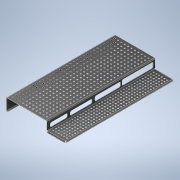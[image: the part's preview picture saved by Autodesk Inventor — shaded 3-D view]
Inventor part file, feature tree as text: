
AUTODESK INVENTOR PART (.ipt)
format: ipt  version: 2022 (Build 260153000, 153)  size: 1,057,280 bytes
history: native  units: in
note: dims shown in document units (in); Inventor stores cm internally (conversion verified against a paired STEP export)
features: sheet_metal_op x16, sketch x9, other x9
ambient origin geometry x8: Origin, YZ Plane, XZ Plane, XY Plane, X Axis, Y Axis, Z Axis, Center Point
bodies: Body1 (feature_tree)
feature tree (34):
  sheet_metal_op  "Face2"
  sheet_metal_op  "Flange1"
  sheet_metal_op  "Flange2"
  sheet_metal_op  "Flange3"
  sheet_metal_op  "Flange4"
  sheet_metal_op  "Flange9"
  sketch  "Sketch1"  dims[d2=5.5118in]
  other  "Plate2"
  sketch  "Sketch2"  dims[d3=2.7559in]
  other  "Plate3"
  sheet_metal_op  "Bend1"
  sheet_metal_op  "Corner1"
  sketch  "Sketch3"  dims[d8=0.1181in]
  other  "Plate4"
  sheet_metal_op  "Bend2"
  sheet_metal_op  "Corner2"
  sketch  "Sketch4"  dims[d9=0.1181in]
  other  "Plate5"
  sheet_metal_op  "Bend3"
  sheet_metal_op  "Corner3"
  sketch  "Sketch5"  dims[d10=0.0591in]
  other  "Plate6"
  sheet_metal_op  "Bend4"
  sheet_metal_op  "Corner4"
  sketch  "Sketch11"  dims[d11=0.2362in]
  sketch  "Sketch12"  dims[d12=0.1181in]
  sketch  "Sketch13"  dims[d13=2.7559in d14=90.0deg d15=0.1181in]
  sketch  "Sketch16"  dims[d16=0.4724in d17=0.1181in d18=0.1181in d19=0.1181in d20=0.0591in d21=0.2362in d22=0.1181in d23=11.811in d24=90.0deg d25=0.1181in d26=0.4724in d27=0.1181in d28=0.1181in d29=0.1181in d30=0.0591in d31=0.2362in d32=0.1181in d33=3.5433in d34=90.0deg d35=0.1181in d36=0.4724in d37=0.1181in d38=0.1181in d39=0.1181in d40=0.0591in d41=0.2362in d42=0.1181in d43=0.3937in d44=90.0deg d45=0.1181in d46=0.4724in d47=0.1181in d48=0.1181in d91=31.4961in d92=15.748in d93=1.5748in d94=0.3937in d95=0.5906in d97=0.3937in d98=7.4803in d100=9.0551in d101=0.7874in d102=0.7874in d103=0.9843in d104=0.3937in d105=1.1811in d106=6.399in d107=0.3937in d108=0.1181in d109=0.0in d110=1.378in d111=0.3937in d112=0.9843in d113=0.748in d114=12.2047in d116=0.9843in d117=4.3307in d119=0.9843in d122=0.9843in d123=0.748in d124=0.1181in d125=0.0in d126=0.3937in d128=0.9843in d130=0.5906in d131=14.9606in d133=0.7874in d134=2.3622in d136=0.7874in d141=0.1181in d142=0.0in d147=1.1811in d148=1.1811in d149=0.1181in d150=0.0591in d151=0.2362in d152=0.1181in d153=0.3937in d154=90.0deg d155=0.1181in d156=0.4724in d157=0.1181in d158=0.1181in]
  other  "Plate11"
  sheet_metal_op  "Bend9"
  sheet_metal_op  "Corner9"
  other  "Cut1"
  other  "Cut2"
  other  "Cut3"
